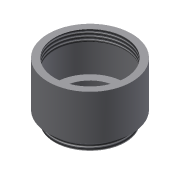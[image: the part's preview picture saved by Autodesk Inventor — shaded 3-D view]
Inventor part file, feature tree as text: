
AUTODESK INVENTOR PART (.ipt)
format: ipt  version: 2013 (Build 170138000, 138)  size: 102,912 bytes
history: native  units: in
note: dims shown in document units (in); Inventor stores cm internally (conversion verified against a paired STEP export)
features: extrude x4, sketch x4, thread x2
ambient origin geometry x8: Origin, YZ Plane, XZ Plane, XY Plane, X Axis, Y Axis, Z Axis, Center Point
bodies: Solid1 (feature_tree)
feature tree (10):
  extrude  "Extrusion1"  Depth=1.0in TaperAngle=0.0deg
  extrude  "Extrusion3"  Depth=0.1969in TaperAngle=0.0deg
  thread  "Thread2"  [1 undecoded]
  extrude  "Extrusion4"  Depth=0.7in TaperAngle=0.0deg
  thread  "Thread3"  [1 undecoded]
  extrude  "Extrusion5"  Depth=0.7in TaperAngle=0.0deg
  sketch  "Sketch1"  dims[d0=1.4961in d1=1.0in d2=0.0in]
  sketch  "Sketch3"  dims[d9=1.2598in d10=0.1969in d11=0.0in d12=1.0in d13=0.0in]
  sketch  "Sketch4"  dims[d14=1.2598in d15=0.7in d16=0.0in d17=0.1969in d18=0.0in]
  sketch  "Sketch5"  dims[d19=0.9843in d20=0.7in d21=0.0in]
note: 2 required parameter values undecoded (feature->parameter linkage not recoverable at this tier; creation-order binding heuristic only, values carry confidence <= 0.55)
